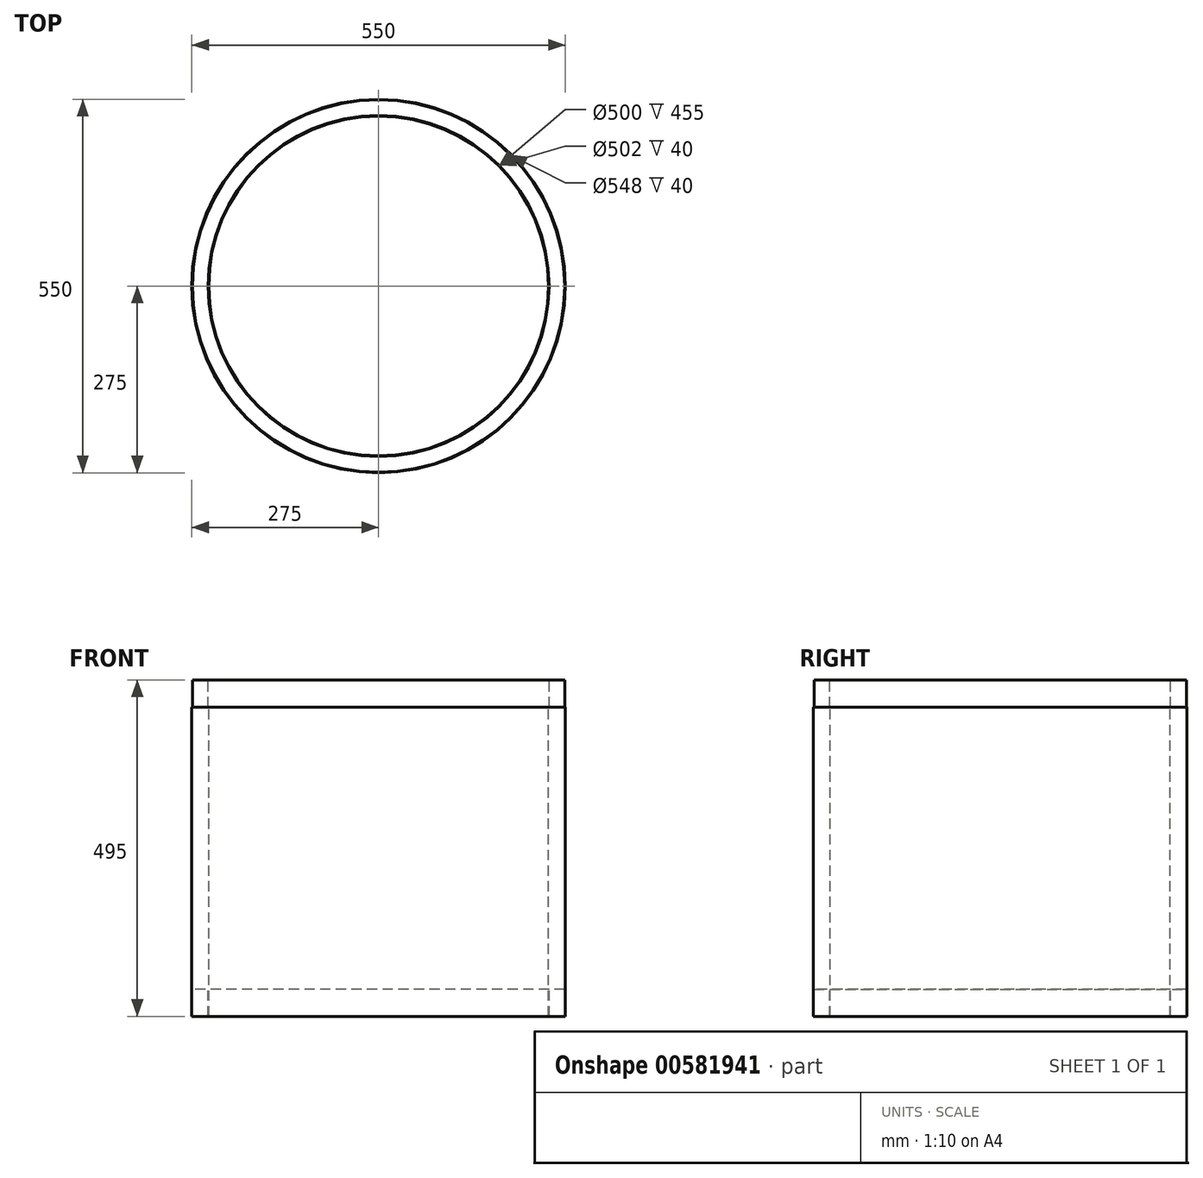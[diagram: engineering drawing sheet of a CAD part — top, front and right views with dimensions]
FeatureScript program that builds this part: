
annotation { "Feature Type Name" : "Feature", "Feature Type Description" : "" }
export const myFeature = defineFeature(function(context is Context, id is Id, definition is map)
    precondition{}
    {
        {
            var Q0;
            Q0=qCreatedBy(makeId("Front.planeOp"),FACE);
            var sketch = newSketch(context, id + "F0", { "sketchPlane" : qUnion([Q0])});
            skLineSegment(sketch, "E0", {"start": v(0, 345.75) * mm, "end": v(0, -558.03) * mm, "construction": true});
            skLineSegment(sketch, "E1", {"start": v(-250, -518.84) * mm, "end": v(-250, -63.84) * mm});
            skLineSegment(sketch, "E2", {"start": v(-250, -63.84) * mm, "end": v(-251, -63.84) * mm});
            skLineSegment(sketch, "E3", {"start": v(-251, -63.84) * mm, "end": v(-251, -23.84) * mm});
            skLineSegment(sketch, "E4", {"start": v(-251, -23.84) * mm, "end": v(-274, -23.84) * mm});
            skLineSegment(sketch, "E5", {"start": v(-274, -23.84) * mm, "end": v(-274, -63.84) * mm});
            skLineSegment(sketch, "E6", {"start": v(-274, -63.84) * mm, "end": v(-275, -63.84) * mm});
            skLineSegment(sketch, "E7", {"start": v(-275, -63.84) * mm, "end": v(-275, -518.84) * mm});
            skLineSegment(sketch, "E8", {"start": v(-275, -518.84) * mm, "end": v(-274, -518.84) * mm});
            skLineSegment(sketch, "E9", {"start": v(-274, -518.84) * mm, "end": v(-274, -478.84) * mm});
            skLineSegment(sketch, "E10", {"start": v(-274, -478.84) * mm, "end": v(-251, -478.84) * mm});
            skLineSegment(sketch, "E11", {"start": v(-251, -478.84) * mm, "end": v(-251, -518.84) * mm});
            skLineSegment(sketch, "E12", {"start": v(-251, -518.84) * mm, "end": v(-250, -518.84) * mm});
            skSolve(sketch);
        }
        {
            var Q0;
            Q0=qSketchRegion(id+"F0",true);
            var Q1;
            Q1=sQuery(id+"F0.wireOp",EDGE,"E0");
            revolve(context, id + "F1", {"entities" : qUnion([Q0]), "axis" : qUnion([Q1]), "revolveType" : RevolveType.FULL});
        }
    });
